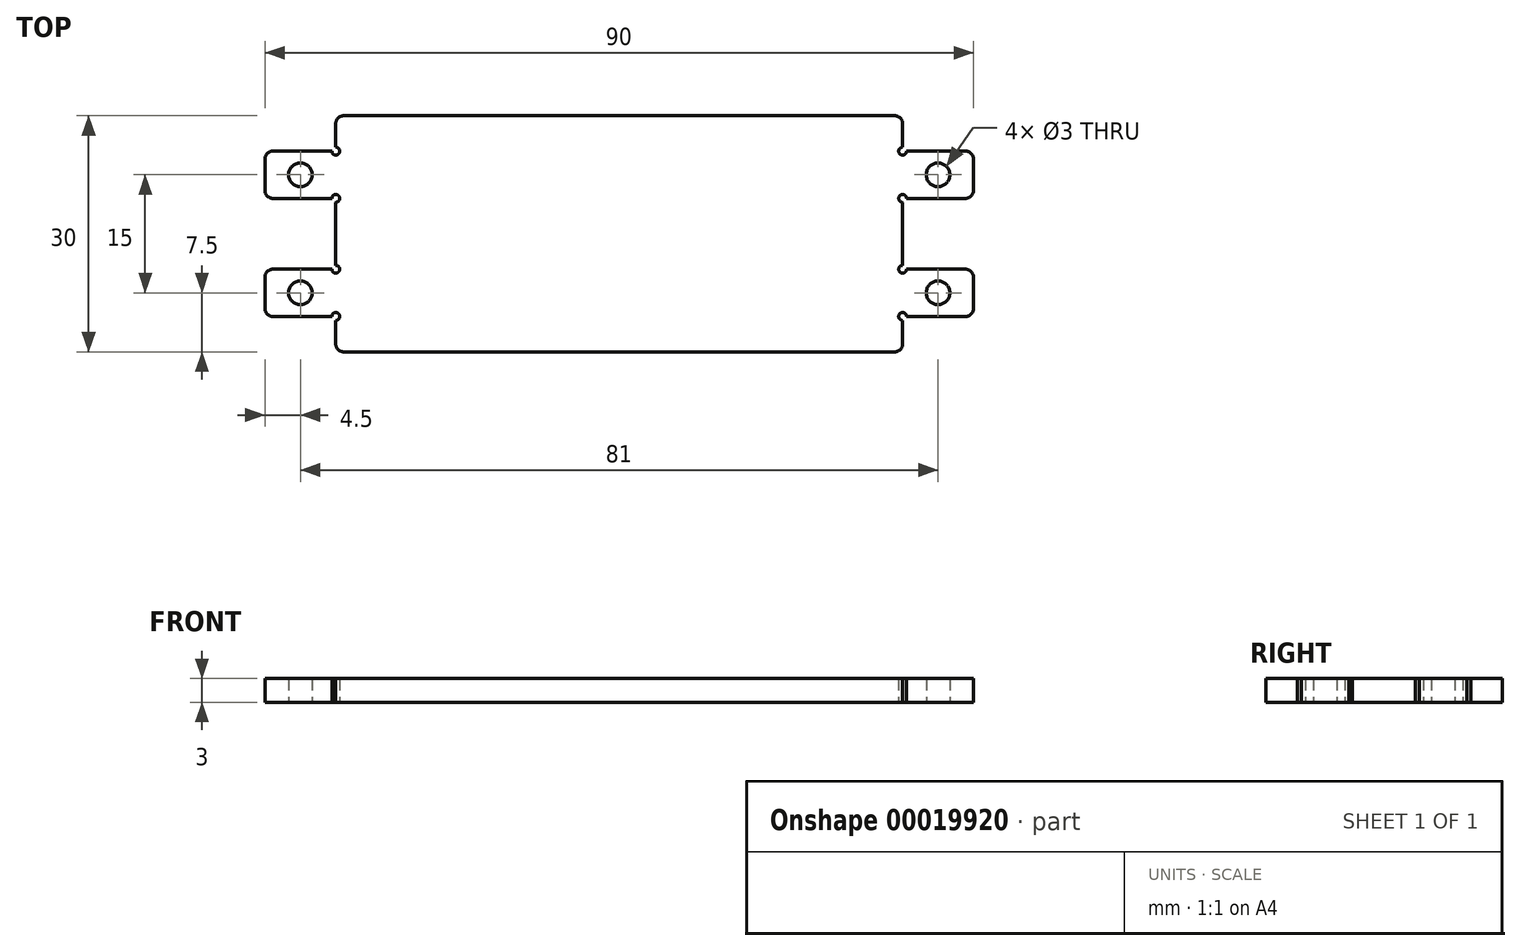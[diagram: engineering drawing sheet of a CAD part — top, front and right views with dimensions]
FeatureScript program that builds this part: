
annotation { "Feature Type Name" : "Feature", "Feature Type Description" : "" }
export const myFeature = defineFeature(function(context is Context, id is Id, definition is map)
    precondition{}
    {
        {
            var Q0;
            Q0=qCreatedBy(makeId("Top.planeOp"),FACE);
            var sketch = newSketch(context, id + "F0", { "sketchPlane" : qUnion([Q0])});
            skLineSegment(sketch, "E0.bottom", {"start": v(-35, 15) * mm, "end": v(35, 15) * mm});
            skLineSegment(sketch, "E0.top", {"start": v(-35, -15) * mm, "end": v(35, -15) * mm});
            skLineSegment(sketch, "E0.left", {"start": v(-45, 9.5) * mm, "end": v(-45, 5.5) * mm});
            skLineSegment(sketch, "E0.right", {"start": v(45, 9.5) * mm, "end": v(45, 5.5) * mm});
            skLineSegment(sketch, "E1", {"start": v(0, 0) * mm, "end": v(71.82, 0) * mm, "construction": true});
            skLineSegment(sketch, "E2", {"start": v(0, 0) * mm, "end": v(0, 47.08) * mm, "construction": true});
            skLineSegment(sketch, "E3.bottom", {"start": v(-44, 10.5) * mm, "end": v(-36.5, 10.5) * mm});
            skLineSegment(sketch, "E3.top", {"start": v(-44, 4.5) * mm, "end": v(-36.5, 4.5) * mm});
            skLineSegment(sketch, "E4.bottom", {"start": v(-44, -4.5) * mm, "end": v(-36.5, -4.5) * mm});
            skLineSegment(sketch, "E4.top", {"start": v(-44, -10.5) * mm, "end": v(-36.5, -10.5) * mm});
            skLineSegment(sketch, "E4.left", {"start": v(-45, -5.5) * mm, "end": v(-45, -9.5) * mm});
            skLineSegment(sketch, "E5.bottom", {"start": v(44, 10.5) * mm, "end": v(36.5, 10.5) * mm});
            skLineSegment(sketch, "E5.top", {"start": v(44, 4.5) * mm, "end": v(36.5, 4.5) * mm});
            skLineSegment(sketch, "E6.bottom", {"start": v(44, -4.5) * mm, "end": v(36.5, -4.5) * mm});
            skLineSegment(sketch, "E6.top", {"start": v(44, -10.5) * mm, "end": v(36.5, -10.5) * mm});
            skLineSegment(sketch, "E6.left", {"start": v(45, -5.5) * mm, "end": v(45, -9.5) * mm});
            skLineSegment(sketch, "E7", {"start": v(-36, 11) * mm, "end": v(-36, 14) * mm});
            skLineSegment(sketch, "E8", {"start": v(-36, 4) * mm, "end": v(-36, -4) * mm});
            skLineSegment(sketch, "E9", {"start": v(-36, -11) * mm, "end": v(-36, -14) * mm});
            skLineSegment(sketch, "E10", {"start": v(36, -11) * mm, "end": v(36, -14) * mm});
            skLineSegment(sketch, "E11", {"start": v(36, -4) * mm, "end": v(36, 4) * mm});
            skLineSegment(sketch, "E12", {"start": v(36, 11) * mm, "end": v(36, 14) * mm});
            skArc(sketch, "E13", {"start": v(-36.5, 10.5) * mm, "mid": v(-35.65, 10.15) * mm, "end": v(-36, 11) * mm});
            skArc(sketch, "E14", {"start": v(-36, 4) * mm, "mid": v(-35.65, 4.85) * mm, "end": v(-36.5, 4.5) * mm});
            skArc(sketch, "E15", {"start": v(-36.5, -4.5) * mm, "mid": v(-35.65, -4.85) * mm, "end": v(-36, -4) * mm});
            skArc(sketch, "E16", {"start": v(-36, -11) * mm, "mid": v(-35.65, -10.15) * mm, "end": v(-36.5, -10.5) * mm});
            skArc(sketch, "E17", {"start": v(36, 11) * mm, "mid": v(35.65, 10.15) * mm, "end": v(36.5, 10.5) * mm});
            skArc(sketch, "E18", {"start": v(36.5, 4.5) * mm, "mid": v(35.65, 4.85) * mm, "end": v(36, 4) * mm});
            skArc(sketch, "E19", {"start": v(36, -4) * mm, "mid": v(35.65, -4.85) * mm, "end": v(36.5, -4.5) * mm});
            skArc(sketch, "E20", {"start": v(36.5, -10.5) * mm, "mid": v(35.65, -10.15) * mm, "end": v(36, -11) * mm});
            skCircle(sketch, "E21", {"center": v(-40.5, 7.5) * mm, "radius": 1.5 * mm});
            skCircle(sketch, "E22", {"center": v(-40.5, -7.5) * mm, "radius": 1.5 * mm});
            skCircle(sketch, "E23", {"center": v(40.5, 7.5) * mm, "radius": 1.5 * mm});
            skCircle(sketch, "E24", {"center": v(40.5, -7.5) * mm, "radius": 1.5 * mm});
            skPoint(sketch, "E25.visualSharp", {"position": v(-45, 10.5) * mm});
            skArc(sketch, "E25.filletArc", {"start": v(-44, 10.5) * mm, "mid": v(-44.7, 10.2) * mm, "end": v(-45, 9.5) * mm});
            skPoint(sketch, "E26.visualSharp", {"position": v(-45, 4.5) * mm});
            skArc(sketch, "E26.filletArc", {"start": v(-45, 5.5) * mm, "mid": v(-44.7, 4.8) * mm, "end": v(-44, 4.5) * mm});
            skPoint(sketch, "E27.visualSharp", {"position": v(-45, -4.5) * mm});
            skArc(sketch, "E27.filletArc", {"start": v(-44, -4.5) * mm, "mid": v(-44.7, -4.8) * mm, "end": v(-45, -5.5) * mm});
            skPoint(sketch, "E28.visualSharp", {"position": v(-45, -10.5) * mm});
            skArc(sketch, "E28.filletArc", {"start": v(-45, -9.5) * mm, "mid": v(-44.7, -10.2) * mm, "end": v(-44, -10.5) * mm});
            skPoint(sketch, "E29.visualSharp", {"position": v(-36, -15) * mm});
            skArc(sketch, "E29.filletArc", {"start": v(-36, -14) * mm, "mid": v(-35.7, -14.7) * mm, "end": v(-35, -15) * mm});
            skPoint(sketch, "E30.visualSharp", {"position": v(-36, 15) * mm});
            skArc(sketch, "E30.filletArc", {"start": v(-35, 15) * mm, "mid": v(-35.7, 14.7) * mm, "end": v(-36, 14) * mm});
            skPoint(sketch, "E31.visualSharp", {"position": v(36, 15) * mm});
            skArc(sketch, "E31.filletArc", {"start": v(36, 14) * mm, "mid": v(35.7, 14.7) * mm, "end": v(35, 15) * mm});
            skPoint(sketch, "E32.visualSharp", {"position": v(36, -15) * mm});
            skArc(sketch, "E32.filletArc", {"start": v(35, -15) * mm, "mid": v(35.7, -14.7) * mm, "end": v(36, -14) * mm});
            skPoint(sketch, "E33.visualSharp", {"position": v(45, -10.5) * mm});
            skArc(sketch, "E33.filletArc", {"start": v(44, -10.5) * mm, "mid": v(44.7, -10.2) * mm, "end": v(45, -9.5) * mm});
            skPoint(sketch, "E34.visualSharp", {"position": v(45, -4.5) * mm});
            skArc(sketch, "E34.filletArc", {"start": v(45, -5.5) * mm, "mid": v(44.7, -4.8) * mm, "end": v(44, -4.5) * mm});
            skPoint(sketch, "E35.visualSharp", {"position": v(45, 4.5) * mm});
            skArc(sketch, "E35.filletArc", {"start": v(44, 4.5) * mm, "mid": v(44.7, 4.8) * mm, "end": v(45, 5.5) * mm});
            skPoint(sketch, "E36.visualSharp", {"position": v(45, 10.5) * mm});
            skArc(sketch, "E36.filletArc", {"start": v(45, 9.5) * mm, "mid": v(44.7, 10.2) * mm, "end": v(44, 10.5) * mm});
            skSolve(sketch);
        }
        {
            var Q0;
            Q0 = qSketchRegion(id + "F0", true);
            extrude(context, id + "F1", {"entities" : qUnion([Q0]), "depth" : 3 * mm});
        }
    });
